# Revit family: Gira_257200
name_source: partatom
category: Elektroinstallationen
revit_build: Autodesk Revit 2017 (Build: 20160225_1515(x64)
units: mm (PartAtom-declared; Revit-internal decimal feet)

## family parameters
Basisbauteil = Fläche
Beim Laden mit Abzugskörper schneiden = Nein
Bemaßung runder Anschluss = Durchmesser verwenden
Beschriftungsausrichtung beibehalten = Nein
Gemeinsam genutzt = Nein
Raumberechnungspunkt = Nein
Teiletyp = Normal

## types (1)
- TKS-Repeater REG Türko
    Anzahl der Eingänge = 0
    BIM = https://media.stage.bim.site X1 REG KNX.rfa
    BIMSITE_PRODUCT_ID = 52df534c91ab5ae52374698e5abb2b8be813e452
    Beschreibung = TKS-Repeater  REG Merkmale:  Aktive Komponente zur Erweiterung einer Gira Türkommunikationsanlage mit Audio- und Videofunktion.  Reichweitenverlängerung und Erhöhung der Teilnehmerzahlen bei Verwendung weiterer Steuergeräte.  Verstärkung der Audio- und Datensignale des Türkommunikations-Systems in beide Richtungen. Repeatermodus:  Verbindet zwei Liniensegmente miteinander, zur Verdopplung der Teilnehmerzahl einer Video- oder Audio-Türkommunikationsanlage und der Leitungsreichweite.  Wichtig: Für die Versorgung des zweiten Liniensegments ist ein zusätzliches Steuergerät erforderlich. Mehrgesprächsmodus:  Im Mehrgesprächsmodus wird die gesamte Anlage auf mehrere Linien (eine Hauptlinie, bis zu fünf Nebenlinien) aufgeteilt, welche über TKS-Repeater miteinander verbunden werden.  Jede Linie wird von einem eigenen Steuergerät versorgt.  Im Mehrgesprächsmodus dürfen bis zu fünf TKS-Repeater in einer Anlage verwendet werden.  Hinweise :  Datensicherung   Die Konfiguration des TKS-Repeaters kann auf einer microSD-Karte gesichert werden.  Inbetriebnahme   Die Inbetriebnahme des TKS-Repeaters ist auch ohne microSD-Karte möglich.
    Breite in Teilungseinheiten = 0
    Bussystem Funkbus = Nein
    Bussystem KNX = Nein
    Bussystem KNX-Funk = Nein
    Bussystem LON = Nein
    Bussystem Powernet = Nein
    Datenblatt = https://media.stage.bim.site
    Datenblatt 1 = https://media.stage.bim.site
    Funktion = erweitern
    Funktion Schalten = Nein
    GTIN = 4010337011125
    HAN = 257200
    HeinzeBIM = https://www.heinze.de
    Hersteller = Gira
    Installationstechnik = Bus-System
    Kosten = 0 $
    Max. Anzahl der Jalousieausgänge = 0
    Max. Schaltleistung [Voltampere] = 0
    Mit Busankopplung = Nein
    Mit LED-Anzeige = Nein
    Produktseite = https://media.stage.bim.site
    Typname = TKS-Repeater REG Türko
    URL = https://www.gira.de
    Vor Ort-/Handbedienung = Nein
    Vorgabe-Ansicht = 1219 mm

## geometry (parser evidence)
native form markers: Sweep x2
no freeform markers — native parametric forms only
